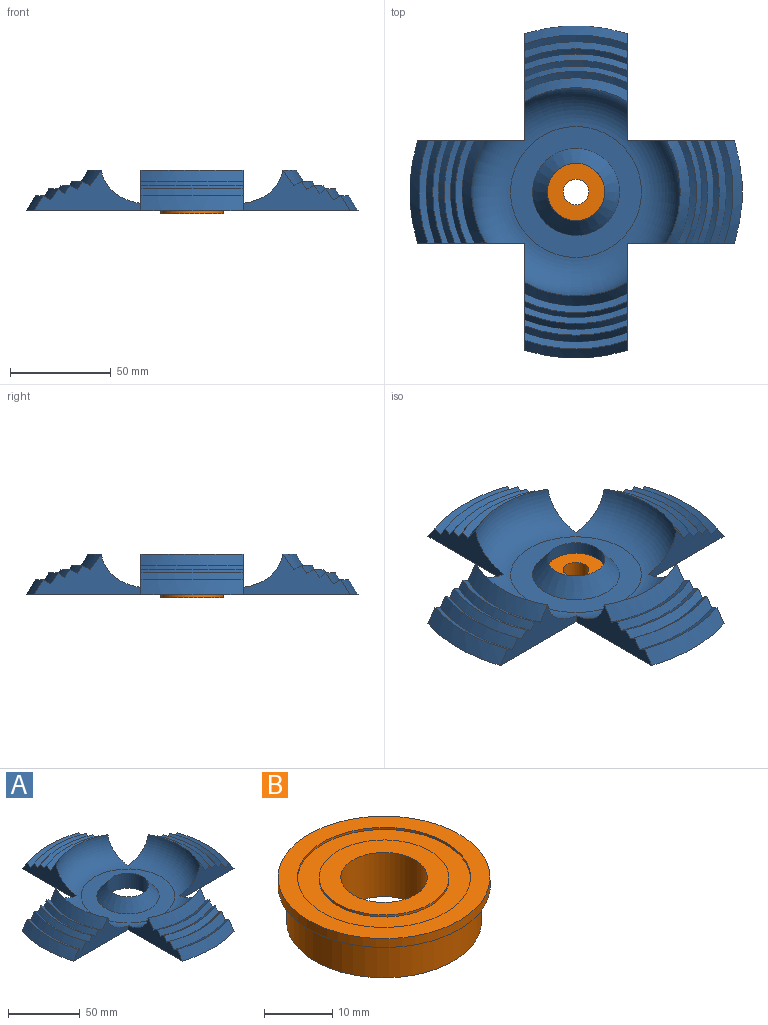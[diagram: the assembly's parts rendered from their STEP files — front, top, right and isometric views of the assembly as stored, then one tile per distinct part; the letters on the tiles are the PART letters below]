
ASSEMBLY  parts=2 mates=1
PART A: 49 faces, bbox 165.6x165.6x23 mm
  f0: torus R=32.54mm, axis (0,0,1), area 6043.1mm2, adj f17,f18,f27,f37,f39,f41,f42,f43
  f1: cone r=78.05mm half-angle=31.8deg, axis (0,0,-1), area 460mm2, adj f3,f28,f41,f47
  f2: cone r=78.05mm half-angle=31.8deg, axis (0,0,-1), area 460mm2, adj f4,f28,f46,f48
  f3: cone r=74.62mm half-angle=58.2deg, axis (0,0,1), area 209.2mm2, adj f1,f5,f41,f47
  f4: cone r=74.62mm half-angle=58.2deg, axis (0,0,1), area 209.2mm2, adj f2,f6,f46,f48
  f5: cone r=71.26mm half-angle=31.8deg, axis (0,0,-1), area 331.3mm2, adj f3,f7,f41,f47
  f6: cone r=71.26mm half-angle=31.8deg, axis (0,0,-1), area 331.3mm2, adj f4,f8,f46,f48
  f7: cone r=68.5mm half-angle=51.7deg, axis (0,0,1), area 183.1mm2, adj f5,f9,f41,f47
  f8: cone r=68.5mm half-angle=51.7deg, axis (0,0,1), area 183.1mm2, adj f6,f10,f46,f48
  f9: cone r=65.5mm half-angle=38.3deg, axis (0,0,-1), area 251.7mm2, adj f7,f11,f41,f47
  f10: cone r=65.5mm half-angle=38.3deg, axis (0,0,-1), area 251.7mm2, adj f8,f12,f46,f48
  f11: cone r=62.49mm half-angle=58.2deg, axis (0,0,1), area 185.3mm2, adj f9,f13,f41,f47
  f12: cone r=62.49mm half-angle=58.2deg, axis (0,0,1), area 185.3mm2, adj f10,f14,f46,f48
  f13: cone r=60.04mm half-angle=31.8deg, axis (0,0,-1), area 244.3mm2, adj f11,f15,f41,f47
  f14: cone r=60.04mm half-angle=31.8deg, axis (0,0,-1), area 244.3mm2, adj f12,f16,f46,f48
  f15: cone r=56.65mm half-angle=58.2deg, axis (0,0,1), area 209.7mm2, adj f13,f17,f41,f47
  f16: cone r=56.65mm half-angle=58.2deg, axis (0,0,1), area 209.7mm2, adj f14,f18,f46,f48
  f17: cone r=51.83mm half-angle=31.8deg, axis (0,0,-1), area 485.1mm2, adj f0,f15,f41,f47
  f18: cone r=51.83mm half-angle=31.8deg, axis (0,0,-1), area 485.1mm2, adj f0,f16,f46,f48
  f19: cone r=78.05mm half-angle=31.8deg, axis (0,0,-1), area 460mm2, adj f20,f28,f44,f45
  f20: cone r=74.62mm half-angle=58.2deg, axis (0,0,1), area 209.2mm2, adj f19,f21,f44,f45
  f21: cone r=71.26mm half-angle=31.8deg, axis (0,0,-1), area 331.3mm2, adj f20,f22,f44,f45
  f22: cone r=68.5mm half-angle=51.7deg, axis (0,0,1), area 183.1mm2, adj f21,f23,f44,f45
  f23: cone r=65.5mm half-angle=38.3deg, axis (0,0,-1), area 251.7mm2, adj f22,f24,f44,f45
  f24: cone r=62.49mm half-angle=58.2deg, axis (0,0,1), area 185.3mm2, adj f23,f25,f44,f45
  f25: cone r=60.04mm half-angle=31.8deg, axis (0,0,-1), area 244.3mm2, adj f24,f26,f44,f45
  f26: cone r=56.65mm half-angle=58.2deg, axis (0,0,1), area 209.7mm2, adj f25,f27,f44,f45
  f27: cone r=51.83mm half-angle=31.8deg, axis (0,0,-1), area 485.1mm2, adj f0,f26,f44,f45
  f28: plane 165.47x165.47mm, normal (0,0,-1), area 13321.8mm2, adj f1,f2,f19,f29,f38,f41,f42,f43
  f29: cone r=78.05mm half-angle=31.8deg, axis (0,0,-1), area 460mm2, adj f28,f30,f42,f43
  f30: cone r=74.62mm half-angle=58.2deg, axis (0,0,1), area 209.2mm2, adj f29,f31,f42,f43
  f31: cone r=71.26mm half-angle=31.8deg, axis (0,0,-1), area 331.3mm2, adj f30,f32,f42,f43
  f32: cone r=68.5mm half-angle=51.7deg, axis (0,0,1), area 183.1mm2, adj f31,f33,f42,f43
  f33: cone r=65.5mm half-angle=38.3deg, axis (0,0,-1), area 251.7mm2, adj f32,f34,f42,f43
  f34: cone r=62.49mm half-angle=58.2deg, axis (0,0,1), area 185.3mm2, adj f33,f35,f42,f43
  f35: cone r=60.04mm half-angle=31.8deg, axis (0,0,-1), area 244.3mm2, adj f34,f36,f42,f43
  f36: cone r=56.65mm half-angle=58.2deg, axis (0,0,1), area 209.7mm2, adj f35,f37,f42,f43
  f37: cone r=51.83mm half-angle=31.8deg, axis (0,0,-1), area 485.1mm2, adj f0,f36,f42,f43
  f38: cylinder r=14.29mm len=28.58mm, axis (0,0,1), area 1140.1mm2, adj f28,f40
  f39: plane 65.08x65.08mm, normal (0,0,1), area 1860.9mm2, adj f0,f40
  f40: cone r=14.29mm half-angle=38.2deg, axis (0,0,-1), area 1335mm2, adj f38,f39
  f41: plane 53.47x20.39mm, normal (1,0,0), area 506.6mm2, adj f0,f1,f3,f5,f7,f9,f11,f13
  f42: plane 53.47x20.39mm, normal (0,-1,0), area 506.6mm2, adj f0,f28,f29,f30,f31,f32,f33,f34
  f43: plane 53.47x20.39mm, normal (0,1,0), area 506.6mm2, adj f0,f28,f29,f30,f31,f32,f33,f34
  f44: plane 53.47x20.39mm, normal (1,0,0), area 506.6mm2, adj f0,f19,f20,f21,f22,f23,f24,f25
  f45: plane 53.47x20.39mm, normal (-1,0,0), area 506.6mm2, adj f0,f19,f20,f21,f22,f23,f24,f25
  f46: plane 53.47x20.39mm, normal (0,1,0), area 506.6mm2, adj f0,f2,f4,f6,f8,f10,f12,f14
  f47: plane 53.47x20.39mm, normal (-1,0,0), area 506.6mm2, adj f0,f1,f3,f5,f7,f9,f11,f13
  f48: plane 53.47x20.39mm, normal (0,-1,0), area 506.6mm2, adj f0,f2,f4,f6,f8,f10,f12,f14
PART B: 10 faces, bbox 31.1x31.1x7.9 mm
  f0: cylinder r=12.7mm len=25.4mm, axis (0,0,1), area 30.4mm2, adj f8,f9
  f1: cylinder r=15.56mm len=31.12mm, axis (0,0,1), area 155.2mm2, adj f7,f8
  f2: cylinder r=14.29mm len=28.58mm, axis (0,0,1), area 570mm2, adj f6,f7
  f3: cylinder r=6.35mm len=12.7mm, axis (0,0,1), area 316.7mm2, adj f5,f6
  f4: cylinder r=9.53mm len=19.05mm, axis (0,0,1), area 22.8mm2, adj f5,f9
  f5: plane 19.05x19.05mm, normal (0,0,1), area 158.3mm2, adj f3,f4
  f6: plane 28.58x28.58mm, normal (0,0,-1), area 514.6mm2, adj f2,f3
  f7: plane 31.12x31.12mm, normal (0,0,-1), area 119.1mm2, adj f1,f2
  f8: plane 31.12x31.12mm, normal (0,0,1), area 253.7mm2, adj f0,f1
  f9: plane 25.4x25.4mm, normal (0,0,1), area 221.7mm2, adj f0,f4
PLACE A t=(-5,-1.04,-1.41)mm
PLACE B rot(axis=(1,0,0),180deg) t=(-5,-1.04,-1.78)mm
MATE fastened B.f0 <-> A.f0  axis (0,0,1) through (-5,-1.04,-8.13)mm
